# Revit family: New Square Touch
name_source: partatom
category: Equipamento especial
revit_build: Autodesk Revit 2016 (Build: 20150220_1215(x64)
units: mm (PartAtom-declared; Revit-internal decimal feet)

## family parameters
Com base no plano de trabalho = Não
Compartilhado = Não
Corte com vazios quando carregados = Não
Cota do conector redondo = Utilizar diâmetro
Ponto de cálculo do ambiente = Não
Sempre na vertical = Sim
Tipo de parte = Normal

## types (1)
- Tramontina - New Square Touch
    Classe de Construção = Classe 1
    Consumo máximo = 6,9 kWh
    Código de montagem = 94751/220
    Descrição = Tramontina Cooktop por Indução - 94751-220
    Desenvolvedor = Factory Cursos & Desenvolvimento
    Disjuntor termomagnético = 32 A
    Fabricante = Tramontina
    Frequência = 50 - 60 Hz
    Grau de  construção = IPX0
    Modelo = Tramontina - New Square Touch B 4EI 60
    Nicho de Instalação = 565 x 495
    Potência das áreas de aquecimento - 200 mm Diametro (1x) = 1,7 kW (2x)
    Potência máxima = 6,9 kW
    Potência áreas de aquecimento - 160 mm (3X) Diametro = 1,5 kW (3x)
    Site do desenvolvedor = www.factorycursos.com.br
    Tensão = 220 V
    Tipo de imagem = NEW SQUARE TOUCH B 4EL 60_IMAGEM 2.jpg
    URL = www.tramontina.com.br
